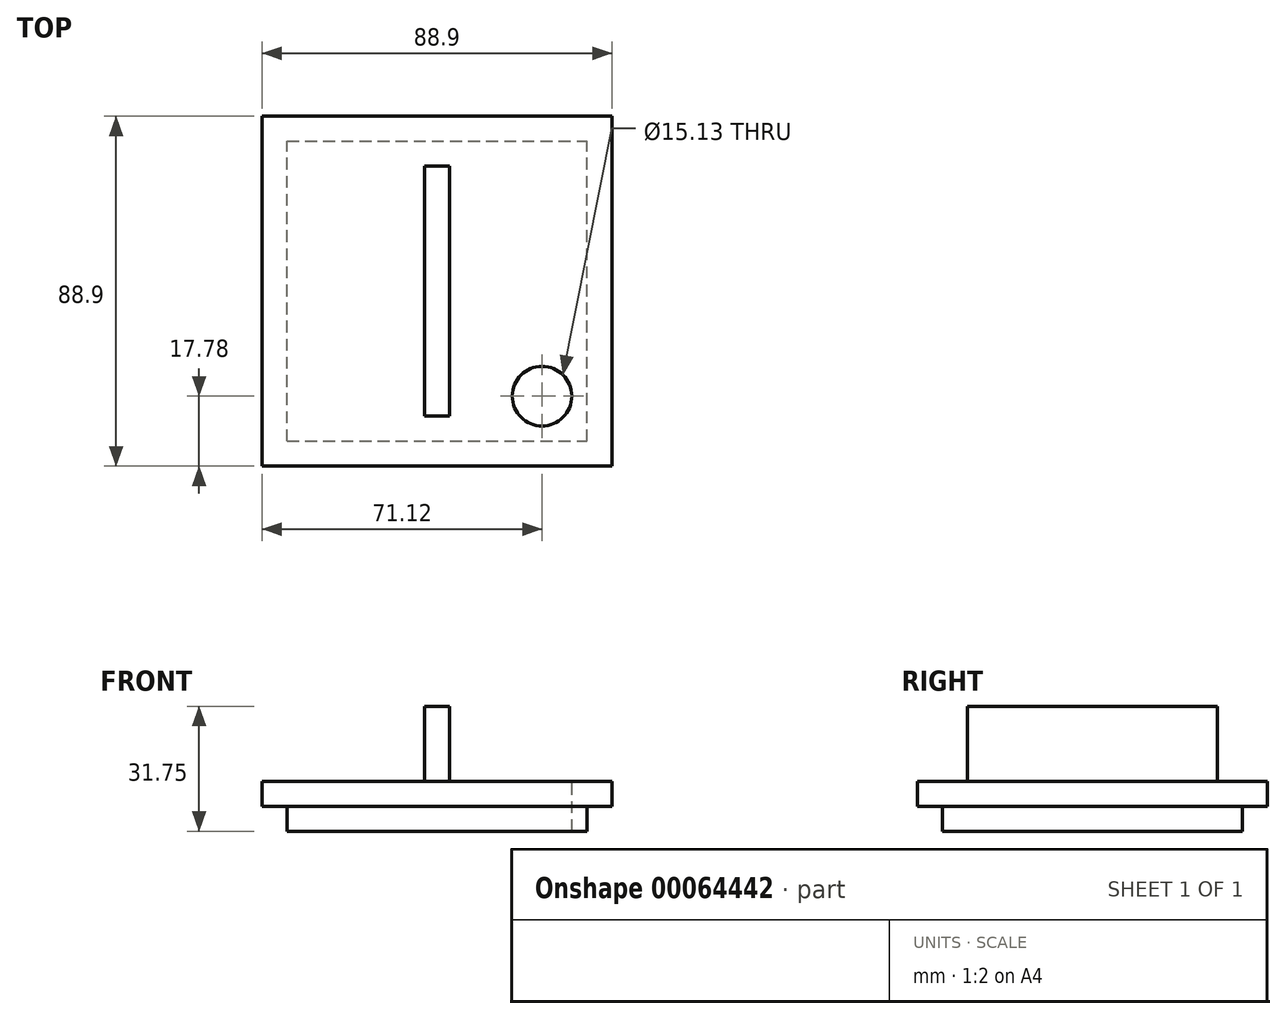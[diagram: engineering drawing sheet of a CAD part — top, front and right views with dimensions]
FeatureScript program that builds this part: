
annotation { "Feature Type Name" : "Feature", "Feature Type Description" : "" }
export const myFeature = defineFeature(function(context is Context, id is Id, definition is map)
    precondition{}
    {
        {
            var Q0;
            Q0=qCreatedBy(makeId("Top.planeOp"),FACE);
            var sketch = newSketch(context, id + "F0", { "sketchPlane" : qUnion([Q0])});
            skLineSegment(sketch, "E0.rect.bottom", {"start": v(-44.45, 44.45) * mm, "end": v(44.45, 44.45) * mm});
            skLineSegment(sketch, "E0.rect.top", {"start": v(-44.45, -44.45) * mm, "end": v(44.45, -44.45) * mm});
            skLineSegment(sketch, "E0.rect.left", {"start": v(-44.45, 44.45) * mm, "end": v(-44.45, -44.45) * mm});
            skLineSegment(sketch, "E0.rect.right", {"start": v(44.45, 44.45) * mm, "end": v(44.45, -44.45) * mm});
            skPoint(sketch, "E0.rect.middle", {"position": v(0, 0) * mm});
            skSolve(sketch);
        }
        {
            var Q0;
            Q0 = qSketchRegion(id + "F0", true);
            extrude(context, id + "F1", {"entities" : qUnion([Q0]), "depth" : 6.35 * mm});
        }
        {
            var Q0;
            Q0=makeQuery(id+"F1.opExtrude","CAP_FACE",FACE,{"disambiguationData":[OSD([sQuery(id+"F0.wireOp",EDGE,"E0.rect.bottom"),sQuery(id+"F0.wireOp",EDGE,"E0.rect.top"),sQuery(id+"F0.wireOp",EDGE,"E0.rect.left"),sQuery(id+"F0.wireOp",EDGE,"E0.rect.right")])],"isStart":true});
            var sketch = newSketch(context, id + "F2", { "sketchPlane" : qUnion([Q0])});
            skLineSegment(sketch, "E1.rect.bottom", {"start": v(-38.1, 38.1) * mm, "end": v(38.1, 38.1) * mm});
            skLineSegment(sketch, "E1.rect.top", {"start": v(-38.1, -38.1) * mm, "end": v(38.1, -38.1) * mm});
            skLineSegment(sketch, "E1.rect.left", {"start": v(-38.1, 38.1) * mm, "end": v(-38.1, -38.1) * mm});
            skLineSegment(sketch, "E1.rect.right", {"start": v(38.1, 38.1) * mm, "end": v(38.1, -38.1) * mm});
            skPoint(sketch, "E1.rect.middle", {"position": v(0, 0) * mm});
            skSolve(sketch);
        }
        {
            var Q0;
            Q0 = qSketchRegion(id + "F2", true);
            extrude(context, id + "F3", {"entities" : qUnion([Q0]), "operationType" : NewBodyOperationType.ADD, "depth" : 6.35 * mm});
        }
        {
            var Q0;
            Q0=makeQuery(id+"F1.opExtrude","CAP_FACE",FACE,{"disambiguationData":[OSD([sQuery(id+"F0.wireOp",EDGE,"E0.rect.bottom"),sQuery(id+"F0.wireOp",EDGE,"E0.rect.top"),sQuery(id+"F0.wireOp",EDGE,"E0.rect.left"),sQuery(id+"F0.wireOp",EDGE,"E0.rect.right")])],"isStart":false});
            var sketch = newSketch(context, id + "F4", { "sketchPlane" : qUnion([Q0])});
            skLineSegment(sketch, "E2.rect.bottom", {"start": v(-3.17, 31.75) * mm, "end": v(3.18, 31.75) * mm});
            skLineSegment(sketch, "E2.rect.top", {"start": v(-3.18, -31.75) * mm, "end": v(3.17, -31.75) * mm});
            skLineSegment(sketch, "E2.rect.left", {"start": v(-3.17, 31.75) * mm, "end": v(-3.18, -31.75) * mm});
            skLineSegment(sketch, "E2.rect.right", {"start": v(3.18, 31.75) * mm, "end": v(3.17, -31.75) * mm});
            skPoint(sketch, "E2.rect.middle", {"position": v(0, 0) * mm});
            skSolve(sketch);
        }
        {
            var Q0;
            Q0 = qSketchRegion(id + "F4", true);
            extrude(context, id + "F5", {"entities" : qUnion([Q0]), "operationType" : NewBodyOperationType.ADD, "depth" : 19.05 * mm});
        }
        {
            var Q0;
            Q0=makeQuery(id+"F1.opExtrude","CAP_FACE",FACE,{"disambiguationData":[OSD([sQuery(id+"F0.wireOp",EDGE,"E0.rect.bottom"),sQuery(id+"F0.wireOp",EDGE,"E0.rect.top"),sQuery(id+"F0.wireOp",EDGE,"E0.rect.left"),sQuery(id+"F0.wireOp",EDGE,"E0.rect.right")])],"isStart":false});
            var sketch = newSketch(context, id + "F6", { "sketchPlane" : qUnion([Q0])});
            skCircle(sketch, "E3", {"center": v(26.67, -26.67) * mm, "radius": 7.57 * mm});
            skSolve(sketch);
        }
        {
            var Q0;
            Q0 = qSketchRegion(id + "F6", true);
            extrude(context, id + "F7", {"entities" : qUnion([Q0]), "operationType" : NewBodyOperationType.REMOVE, "oppositeDirection" : true, "depth" : 25.4 * mm});
        }
    });
